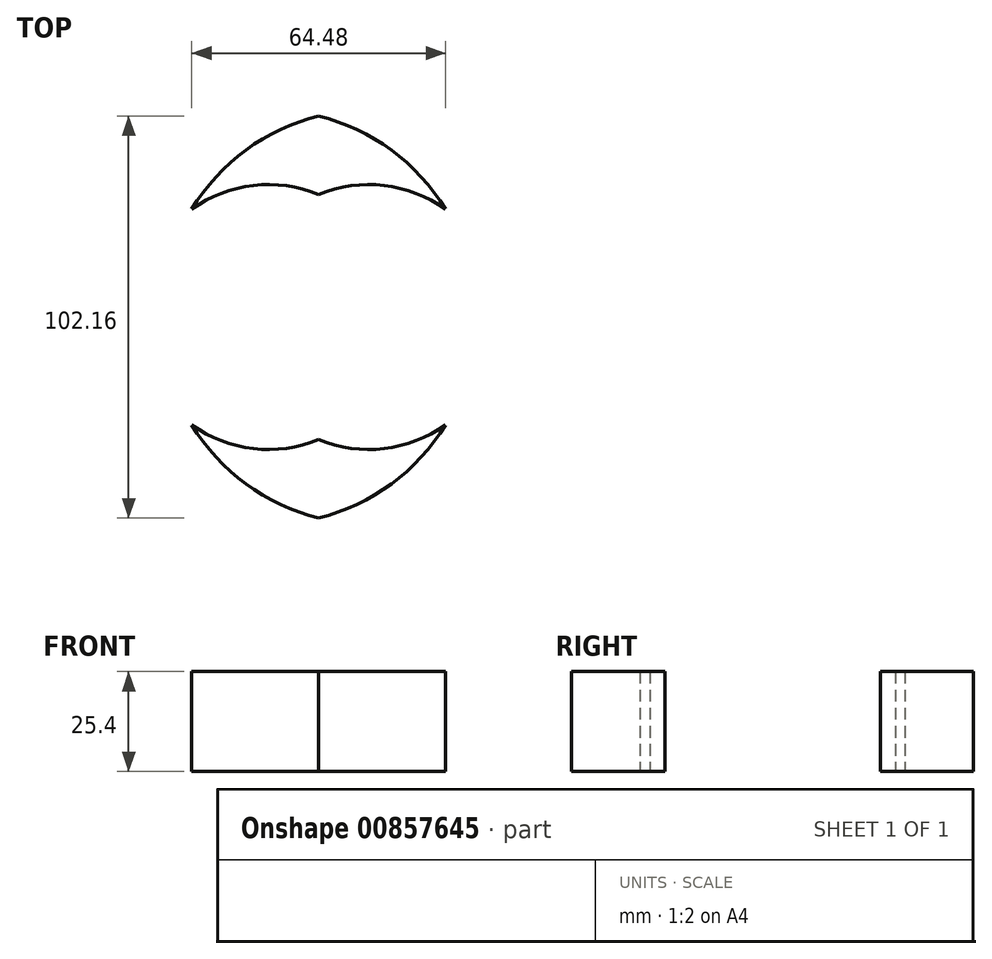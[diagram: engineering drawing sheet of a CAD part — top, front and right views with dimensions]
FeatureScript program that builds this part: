
annotation { "Feature Type Name" : "Feature", "Feature Type Description" : "" }
export const myFeature = defineFeature(function(context is Context, id is Id, definition is map)
    precondition{}
    {
        {
            var Q0;
            Q0=qCreatedBy(makeId("Top.planeOp"),FACE);
            var sketch = newSketch(context, id + "F0", { "sketchPlane" : qUnion([Q0])});
            skCircle(sketch, "E0", {"center": v(0, 0) * mm, "radius": 52.63 * mm});
            skCircle(sketch, "E1", {"center": v(0, 0) * mm, "radius": 33.65 * mm});
            skSolve(sketch);
        }
        {
            var Q0;
            Q0=makeQuery(id+"F0.imprint","IMPRINT",FACE,{"disambiguationData":[TD([[makeQuery(id+"F0.imprint","IMPRINT",EDGE,{"derivedFrom":sQuery(id+"F0.wireOp",EDGE,"E0")}),1.0]])]});
            extrude(context, id + "F1", {"entities" : qUnion([Q0]), "depth" : 25.4 * mm, "offsetDistance" : 25.4 * mm});
        }
        {
            var Q0;
            Q0=makeQuery(id+"F1.opExtrude","SWEPT_BODY",BODY,{"disambiguationData":[OSD([sQuery(id+"F0.wireOp",EDGE,"E0"),sQuery(id+"F0.wireOp",EDGE,"E1")])]});
            transform(context, id + "F2", {"entities" : qUnion([Q0]), "transformType" : TransformType.TRANSLATION_3D, "dx" : 25.4 * mm, "dy" : 0 * mm, "dz" : 0 * mm, "makeCopy" : true});
        }
        {
            var Q0;
            Q0=makeQuery(id+"F1.opExtrude","SWEPT_BODY",BODY,{"disambiguationData":[OSD([sQuery(id+"F0.wireOp",EDGE,"E0"),sQuery(id+"F0.wireOp",EDGE,"E1")])]});
            var Q1;
            Q1=makeQuery(id+"F2.opPattern","COPY",BODY,{"derivedFrom":makeQuery(id+"F1.opExtrude","SWEPT_BODY",BODY,{"disambiguationData":[OSD([sQuery(id+"F0.wireOp",EDGE,"E0"),sQuery(id+"F0.wireOp",EDGE,"E1")])]}),"instanceName":"1"});
            booleanBodies(context, id + "F3", {"operationType" : BooleanOperationType.INTERSECTION, "tools" : qUnion([Q0, Q1])});
        }
    });
